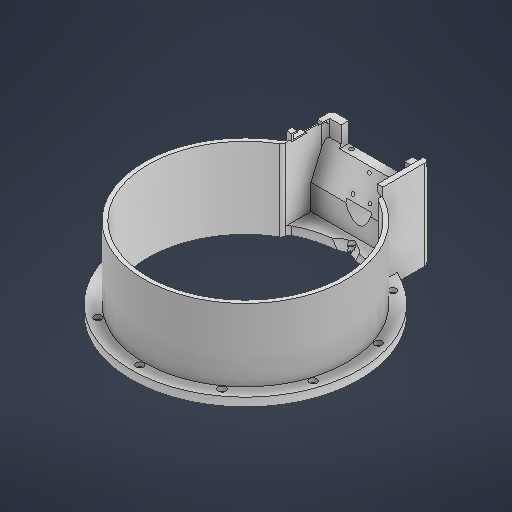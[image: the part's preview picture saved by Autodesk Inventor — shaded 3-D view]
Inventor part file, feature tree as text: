
AUTODESK INVENTOR PART (.ipt)
format: ipt  version: 2025 (Build 290162000, 162)  size: 706,560 bytes
history: native  units: in
note: dims shown in document units (in); Inventor stores cm internally (conversion verified against a paired STEP export)
features: extrude x27, sketch x24, other x3, plane x3, chamfer x3, fillet x1
ambient origin geometry x8: Origin, YZ Plane, XZ Plane, XY Plane, X Axis, Y Axis, Z Axis, Center Point
bodies: Body1 (feature_tree)
feature tree (61):
  other  "Cylinder.ipt"
  extrude  "Extrusion1"  Depth=0.3937in
  extrude  "Extrusion2"  Depth=0.3937in TaperAngle=0.0deg
  sketch  "Sketch3"  dims[d7=11.2205in d8=10.6299in]
  extrude  "Extrusion3"  Depth=10.6299in
  extrude  "Extrusion5"  Depth=0.1969in TaperAngle=0.0deg
  sketch  "Sketch6"  dims[d24=0.1969in d25=0.0in d31=0.0in d32=0.0in]
  extrude  "Extrusion6"  Depth=10.6299in
  extrude  "Extrusion7"  TaperAngle=0.0deg  [1 undecoded]
  extrude  "Extrusion8"  Depth=9.8425in
  plane  "Work Plane1"
  extrude  "Extrusion9"  Depth=10.6299in
  extrude  "Extrusion21"  Depth=0.0787in
  sketch  "Sketch19"  dims[d107=2.2047in d108=0.0in d113=2.5591in]
  extrude  "Extrusion34"  Depth=2.5591in
  extrude  "Extrusion43"  Depth=0.0591in
  extrude  "Extrusion53"  Depth=0.0787in
  extrude  "Extrusion44"  Depth=0.0787in
  extrude  "Extrusion45"  TaperAngle=90.0deg  [1 undecoded]
  chamfer  "Chamfer8"  Distance=1.1614in
  sketch  "Sketch31"  dims[d164=1.5298in d165=0.0787in]
  extrude  "Extrusion46"  Depth=0.0787in
  extrude  "Extrusion47"  Depth=3.937in TaperAngle=360.0deg
  plane  "Work Plane2"
  extrude  "Extrusion48"  Depth=9.065in
  plane  "Work Plane3"
  extrude  "Extrusion51"  Depth=1.8228in
  extrude  "Extrusion54"  Depth=2.564in
  extrude  "Extrusion55"  Depth=3.5433in
  extrude  "Extrusion56"  Depth=3.3661in TaperAngle=0.0deg
  extrude  "Extrusion57"  Depth=3.1496in TaperAngle=0.0deg
  extrude  "Extrusion58"  Depth=0.0787in
  extrude  "Extrusion59"  Depth=0.1575in
  extrude  "Extrusion60"  Depth=0.1575in
  extrude  "Extrusion61"  Depth=0.0787in
  extrude  "Extrusion62"  Depth=0.0787in
  fillet  "Fillet22"  Radius=0.4331in
  chamfer  "Chamfer12"  Distance=0.4331in
  chamfer  "Chamfer13"  Distance=2.1654in
  other  "Solid12::Cylinder.ipt"
  other  "TaggingFeature1"
  sketch  "Sketch1"  dims[d0=0.3937in d2=10.2362in]
  sketch  "Sketch2"  dims[d3=0.0in d4=0.0in d5=0.3937in d6=0.0in]
  sketch  "Sketch5"  dims[d17=10.6299in d18=0.2953in]
  sketch  "Sketch7"  dims[d33=2.1654in d34=0.0in d35=9.8425in]
  sketch  "Sketch9"  dims[d36=10.6299in d46=9.065in]
  sketch  "Sketch14"  dims[d47=0.3937in d48=0.0in d88=0.0787in]
  sketch  "Sketch22"  dims[d117=0.0591in d120=0.5433in]
  sketch  "Sketch Circular Pattern3"  dims[d10=0.1969in d11=0.0in d15=0.1969in d16=0.0in]
  sketch  "Sketch30"  dims[d122=9.4488in d134=0.0787in]
  sketch  "Sketch32"  dims[d166=1.8325in d167=90.0deg d173=1.1614in d174=0.0in]
  sketch  "Sketch35"  dims[d175=0.0787in d209=0.2165in]
  sketch  "Sketch37"  dims[d210=0.3425in d211=3.937in d213=360.0deg]
  sketch  "Sketch38"  dims[d217=10.4151in d218=9.065in]
  sketch  "Sketch39"  dims[d223=0.5433in d224=1.8228in]
  sketch  "Sketch40"  dims[d225=3.5433in d226=2.564in]
  sketch  "Sketch42"  dims[d227=2.7608in d228=3.5433in]
  sketch  "Sketch43"  dims[d233=7.3568in d234=1.5846in d235=0.0in d236=0.0in d237=3.3661in d238=0.3937in d239=0.0in d240=0.0in]
  sketch  "Sketch45"  dims[d241=0.9843in d242=3.1496in d243=0.0in]
  sketch  "Sketch46"  dims[d244=1.5748in d245=0.0787in d246=0.1598in d247=0.4331in]
  sketch  "Sketch47"  dims[d248=0.1575in d249=0.1575in d250=0.1575in d251=0.9331in d255=0.9331in d256=0.4331in d257=0.4331in d258=2.1654in d259=0.0in d260=0.1772in d261=0.0in d263=0.1666in d265=1.5871in d266=0.0in d267=1.5748in d268=0.5315in d269=-3.5433in d277=2.9528in d279=1.5787in d280=0.0in d293=1.378in d306=4.5276in d307=0.0591in d308=2.7608in d309=3.5433in d311=0.3937in d312=0.3937in d313=3.3661in d314=0.3937in d315=0.0in d316=0.0in d317=1.5871in d318=0.0in d319=0.1969in d320=1.1811in d321=0.5906in d322=0.0in d323=0.3937in d324=0.0in d327=0.1772in d328=1.5871in d329=0.0in d330=0.1575in d331=0.0in d332=0.0591in d333=0.1969in d334=0.0in d335=0.2559in d336=0.0in d337=0.0591in d338=0.0591in d339=0.1768in d340=0.0in d341=0.7874in d342=0.0591in d343=0.0591in d344=0.1969in d345=0.0in d346=0.2559in d347=0.0591in d348=0.2559in d349=0.0591in d350=0.1969in d351=0.0in d352=0.1969in d353=0.1575in d354=0.0787in d355=45.0deg d356=0.0787in d357=0.0787in d358=45.0deg d143=0.0197in d144=0.0344in d145=0.0197in d146=0.0344in d153=0.0in d154=0.0in d155=0.0in d156=0.0in d201=0.0197in d202=0.0344in d203=0.0197in d204=0.0344in d215=0.0197in d216=0.0344in d294=0.0197in d295=0.0344in d296=0.0197in d297=0.0344in]
note: 2 required parameter values undecoded (feature->parameter linkage not recoverable at this tier; creation-order binding heuristic only, values carry confidence <= 0.55)
